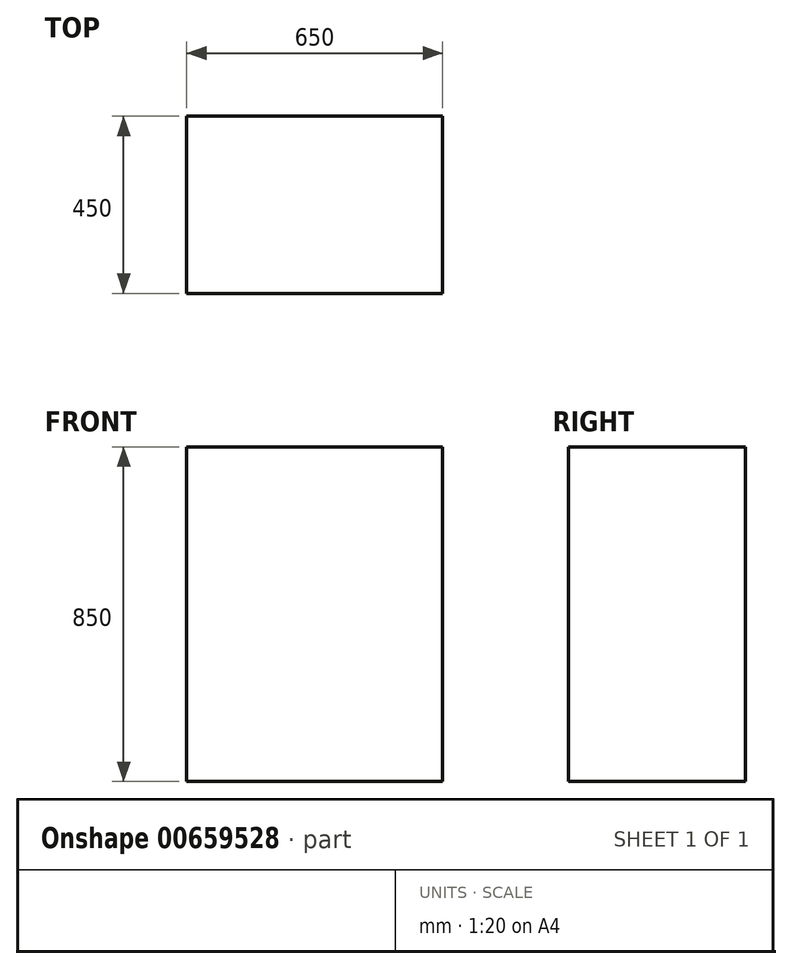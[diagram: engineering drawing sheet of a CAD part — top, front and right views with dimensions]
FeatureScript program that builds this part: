
annotation { "Feature Type Name" : "Feature", "Feature Type Description" : "" }
export const myFeature = defineFeature(function(context is Context, id is Id, definition is map)
    precondition{}
    {
        {
            var Q0;
            Q0=qCreatedBy(makeId("Top.planeOp"),FACE);
            var sketch = newSketch(context, id + "F0", { "sketchPlane" : qUnion([Q0])});
            skLineSegment(sketch, "E0.bottom", {"start": v(-473.3, 127.28) * mm, "end": v(176.7, 127.28) * mm});
            skLineSegment(sketch, "E0.top", {"start": v(-473.3, -322.72) * mm, "end": v(176.7, -322.72) * mm});
            skLineSegment(sketch, "E0.left", {"start": v(-473.3, 127.28) * mm, "end": v(-473.3, -322.72) * mm});
            skLineSegment(sketch, "E0.right", {"start": v(176.7, 127.28) * mm, "end": v(176.7, -322.72) * mm});
            skSolve(sketch);
        }
        {
            var Q0;
            Q0=makeQuery(id+"F0.imprint","IMPRINT",FACE,{"disambiguationData":[TD([[makeQuery(id+"F0.imprint","IMPRINT",EDGE,{"derivedFrom":sQuery(id+"F0.wireOp",EDGE,"E0.bottom")}),-1.0]])]});
            extrude(context, id + "F1", {"entities" : qUnion([Q0]), "depth" : 850 * mm, "offsetDistance" : 25 * mm});
        }
    });
